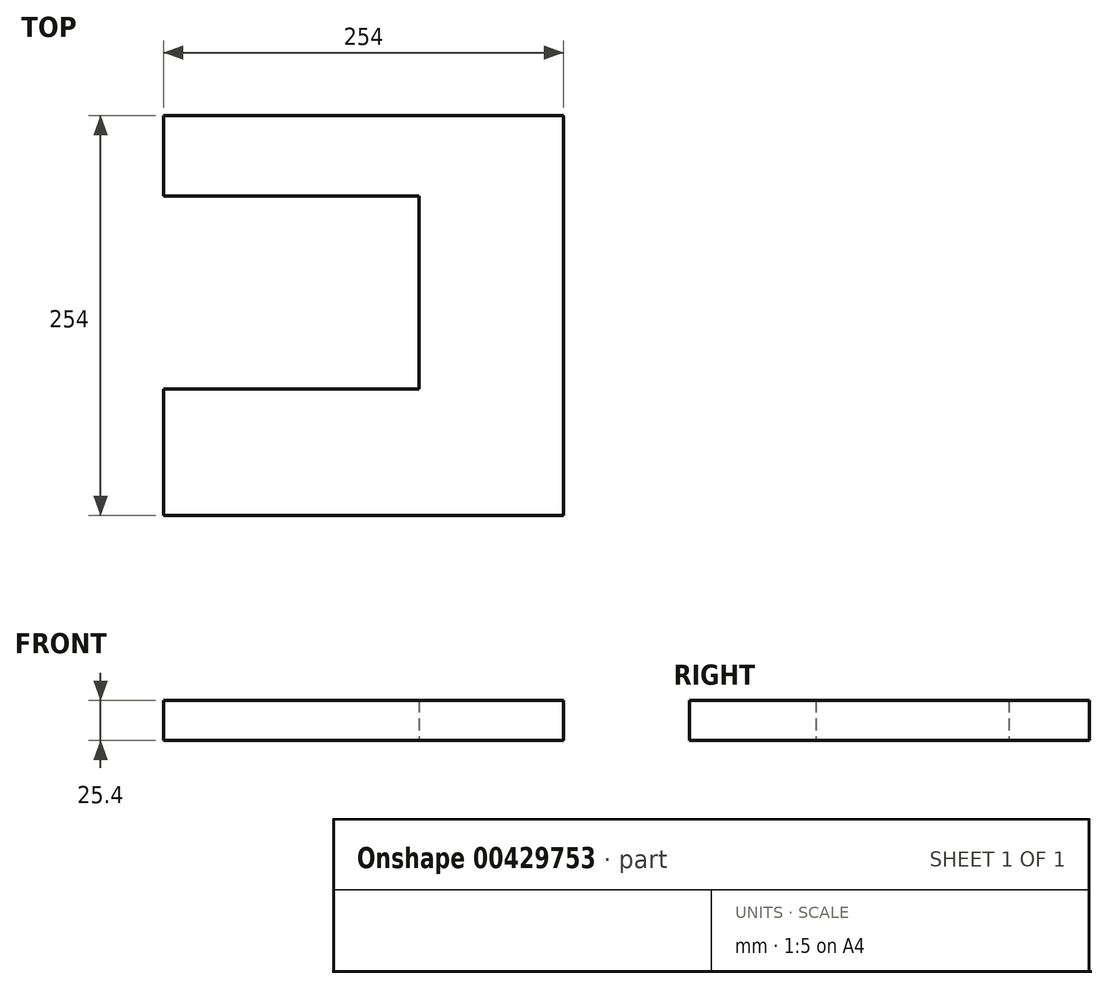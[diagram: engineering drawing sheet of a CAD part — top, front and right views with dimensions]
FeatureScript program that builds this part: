
annotation { "Feature Type Name" : "Feature", "Feature Type Description" : "" }
export const myFeature = defineFeature(function(context is Context, id is Id, definition is map)
    precondition{}
    {
        {
            var Q0;
            Q0=qCreatedBy(makeId("Top.planeOp"),FACE);
            var sketch = newSketch(context, id + "F0", { "sketchPlane" : qUnion([Q0])});
            skLineSegment(sketch, "E0.bottom", {"start": v(127, 127) * mm, "end": v(-127, 127) * mm});
            skLineSegment(sketch, "E0.top", {"start": v(127, -127) * mm, "end": v(-127, -127) * mm});
            skLineSegment(sketch, "E0.left", {"start": v(127, 127) * mm, "end": v(127, -127) * mm});
            skLineSegment(sketch, "E0.right", {"start": v(-127, 127) * mm, "end": v(-127, -127) * mm});
            skPoint(sketch, "E0.middle", {"position": v(0, 0) * mm});
            skLineSegment(sketch, "E1.bottom", {"start": v(-127, 75.79) * mm, "end": v(35.1, 75.79) * mm});
            skLineSegment(sketch, "E1.top", {"start": v(-127, -46.64) * mm, "end": v(35.1, -46.64) * mm});
            skLineSegment(sketch, "E1.left", {"start": v(-127, 75.79) * mm, "end": v(-127, -46.64) * mm});
            skLineSegment(sketch, "E1.right", {"start": v(35.1, 75.79) * mm, "end": v(35.1, -46.64) * mm});
            skSolve(sketch);
        }
        {
            var Q0;
            Q0=makeQuery(id+"F0.imprint","IMPRINT",FACE,{"disambiguationData":[TD([[makeQuery(id+"F0.imprint","IMPRINT",EDGE,{"derivedFrom":sQuery(id+"F0.wireOp",EDGE,"E0.bottom")}),1.0]])]});
            extrude(context, id + "F1", {"entities" : qUnion([Q0]), "depth" : 25.4 * mm});
        }
    });
